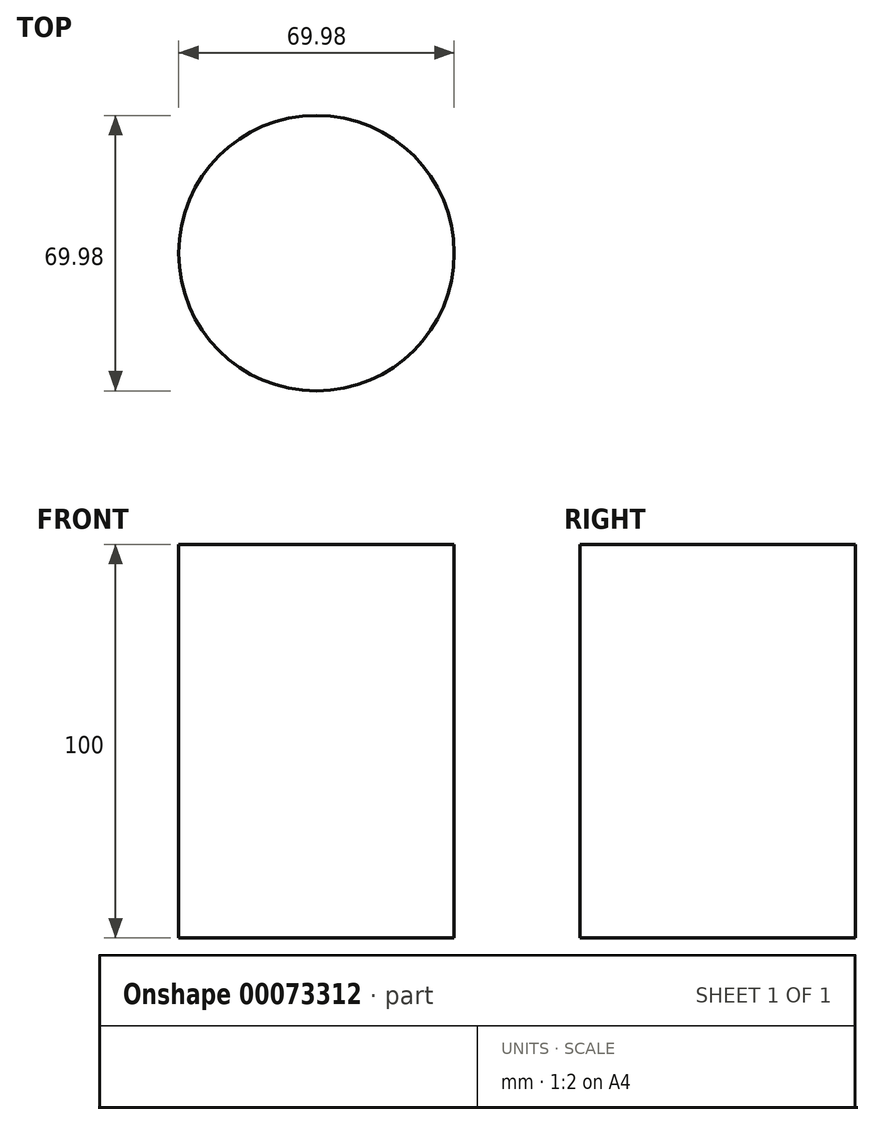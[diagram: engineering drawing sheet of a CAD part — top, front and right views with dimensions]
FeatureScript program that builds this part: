
annotation { "Feature Type Name" : "Feature", "Feature Type Description" : "" }
export const myFeature = defineFeature(function(context is Context, id is Id, definition is map)
    precondition{}
    {
        {
            var Q0;
            Q0=qCreatedBy(makeId("Top.planeOp"),FACE);
            var sketch = newSketch(context, id + "F0", { "sketchPlane" : qUnion([Q0])});
            skCircle(sketch, "E0", {"center": v(0, 0) * mm, "radius": 35 * mm});
            skSolve(sketch);
        }
        {
            var Q0;
            Q0=makeQuery(id+"F0.imprint","IMPRINT",FACE,{"disambiguationData":[TD([[makeQuery(id+"F0.imprint","IMPRINT",EDGE,{"derivedFrom":sQuery(id+"F0.wireOp",EDGE,"E0")}),1.0]])]});
            extrude(context, id + "F1", {"entities" : qUnion([Q0]), "depth" : 100 * mm});
        }
    });
